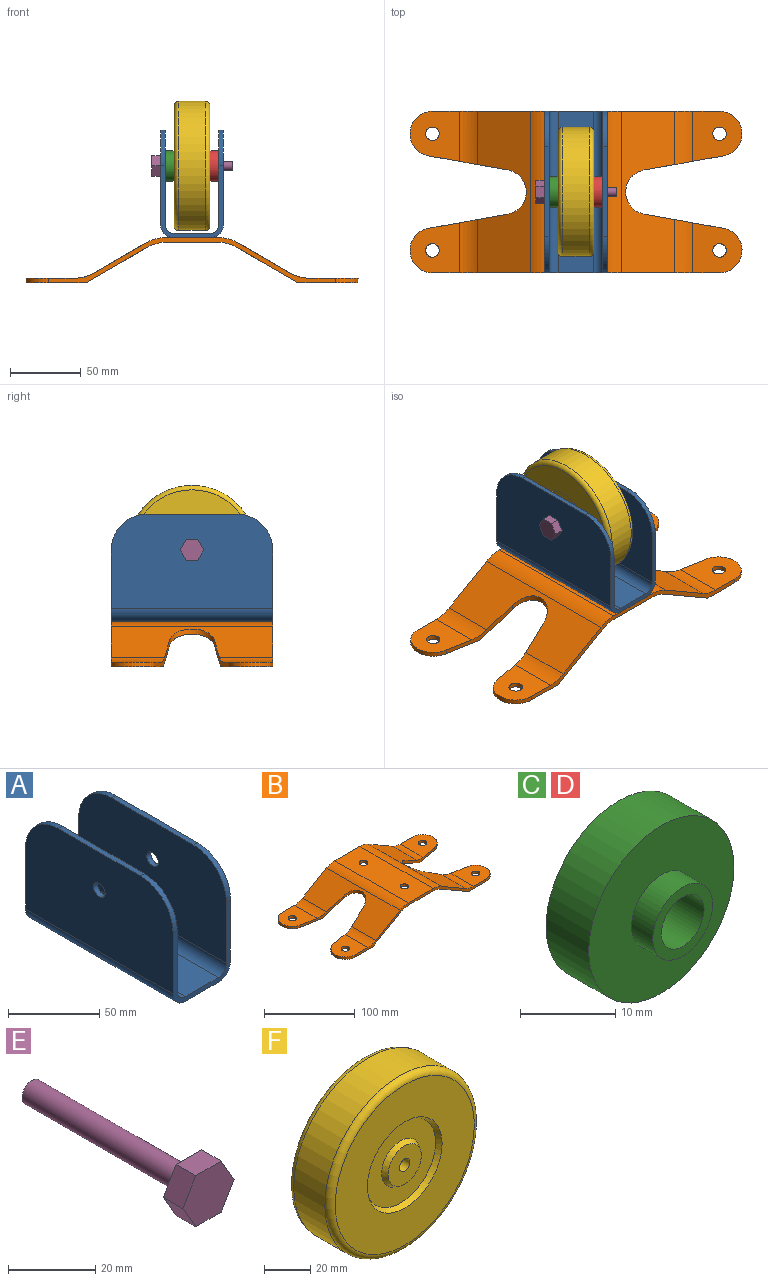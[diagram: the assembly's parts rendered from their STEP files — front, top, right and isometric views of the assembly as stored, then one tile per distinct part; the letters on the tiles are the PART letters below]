
ASSEMBLY  parts=6 mates=11
PART A: 22 faces, bbox 44.5x114.3x76.2 mm
  f0: plane 114.3x25.4mm, normal (0,0,1), area 2760.7mm2, adj f8,f9,f10,f11,f16,f17
  f1: plane 114.3x25.4mm, normal (0,0,-1), area 2760.7mm2, adj f8,f9,f12,f13,f16,f17
  f2: plane 114.3x66.68mm, normal (1,0,0), area 7282mm2, adj f3,f8,f9,f13,f15,f19,f21
  f3: plane 63.5x3.18mm, normal (0,0,1), area 201.6mm2, adj f2,f4,f19,f21
  f4: plane 114.3x66.68mm, normal (-1,0,0), area 7282mm2, adj f3,f8,f9,f10,f15,f19,f21
  f5: plane 114.3x66.68mm, normal (1,0,0), area 7282mm2, adj f6,f8,f9,f11,f14,f18,f20
  f6: plane 63.5x3.18mm, normal (0,0,1), area 201.6mm2, adj f5,f7,f18,f20
  f7: plane 114.3x66.68mm, normal (-1,0,0), area 7282mm2, adj f6,f8,f9,f12,f14,f18,f20
  f8: plane 50.8x44.45mm, normal (0,-1,0), area 421.9mm2, adj f0,f1,f2,f4,f5,f7,f10,f11
  f9: plane 50.8x44.45mm, normal (0,1,0), area 421.9mm2, adj f0,f1,f2,f4,f5,f7,f10,f11
  f10: cylinder r=6.35mm len=114.3mm, axis (0,-1,0), area 1140.1mm2, adj f0,f4,f8,f9
  f11: cylinder r=6.35mm len=114.3mm, axis (0,1,0), area 1140.1mm2, adj f0,f5,f8,f9
  f12: cylinder r=9.53mm len=114.3mm, axis (0,1,0), area 1710.1mm2, adj f1,f7,f8,f9
  f13: cylinder r=9.53mm len=114.3mm, axis (0,-1,0), area 1710.1mm2, adj f1,f2,f8,f9
  f14: cylinder r=4.45mm len=8.89mm, axis (1,0,0), area 88.7mm2, adj f5,f7
  f15: cylinder r=4.45mm len=8.89mm, axis (1,0,0), area 88.7mm2, adj f2,f4
  f16: cylinder r=4.76mm len=9.53mm, axis (0,0,-1), area 95mm2, adj f0,f1
  f17: cylinder r=4.76mm len=9.53mm, axis (0,0,-1), area 95mm2, adj f0,f1
  f18: cylinder r=25.4mm len=25.4mm, axis (-1,0,0), area 126.7mm2, adj f5,f6,f7,f9
  f19: cylinder r=25.4mm len=25.4mm, axis (-1,0,0), area 126.7mm2, adj f2,f3,f4,f9
  f20: cylinder r=25.4mm len=25.4mm, axis (1,0,0), area 126.7mm2, adj f5,f6,f7,f8
  f21: cylinder r=25.4mm len=25.4mm, axis (1,0,0), area 126.7mm2, adj f2,f3,f4,f8
PART B: 40 faces, bbox 235x114.3x31.8 mm
  f0: plane 42.58x36.76mm, normal (0,0,-1), area 1243mm2, adj f2,f8,f15,f16,f17
  f1: plane 42.58x36.76mm, normal (0,0,-1), area 1243mm2, adj f2,f7,f12,f13,f14
  f2: plane 114.3x43.6mm, normal (-0.5,0,-0.87), area 4290.5mm2, adj f0,f1,f12,f14,f15,f17,f18,f39
  f3: plane 114.3x37.19mm, normal (0,0,-1), area 4108.1mm2, adj f12,f17,f21,f22,f38,f39
  f4: plane 114.3x43.6mm, normal (0.5,0,-0.87), area 4290.5mm2, adj f5,f6,f9,f10,f11,f12,f17,f38
  f5: plane 42.58x36.76mm, normal (0,0,-1), area 1243mm2, adj f4,f9,f17,f19,f23
  f6: plane 42.58x36.76mm, normal (0,0,-1), area 1243mm2, adj f4,f11,f12,f20,f24
  f7: cylinder r=4.76mm len=9.53mm, axis (0,0,-1), area 95mm2, adj f1,f31
  f8: cylinder r=4.76mm len=9.53mm, axis (0,0,-1), area 95mm2, adj f0,f25
  f9: plane 55.84x19.06mm, normal (-0.18,0.98,0), area 197.6mm2, adj f4,f5,f10,f19,f28,f30,f37
  f10: cylinder r=15.88mm len=31.26mm, axis (0,0,-1), area 162.3mm2, adj f4,f9,f11,f28
  f11: plane 55.84x19.06mm, normal (-0.18,-0.98,0), area 197.6mm2, adj f4,f6,f10,f20,f28,f29,f33
  f12: plane 203.2x31.75mm, normal (0,1,0), area 701.7mm2, adj f1,f2,f3,f4,f6,f13,f20,f26
  f13: cylinder r=15.88mm len=31.56mm, axis (0,0,-1), area 150.5mm2, adj f1,f12,f14,f31
  f14: plane 55.84x19.06mm, normal (0.18,-0.98,0), area 197.6mm2, adj f1,f2,f13,f18,f26,f31,f32
  f15: plane 55.84x19.06mm, normal (0.18,0.98,0), area 197.6mm2, adj f0,f2,f16,f18,f25,f26,f34
  f16: cylinder r=15.88mm len=31.56mm, axis (0,0,-1), area 150.5mm2, adj f0,f15,f17,f25
  f17: plane 203.2x31.75mm, normal (0,-1,0), area 701.7mm2, adj f0,f2,f3,f4,f5,f16,f19,f25
  f18: cylinder r=15.88mm len=31.26mm, axis (0,0,-1), area 162.3mm2, adj f2,f14,f15,f26
  f19: cylinder r=15.88mm len=31.56mm, axis (0,0,-1), area 150.5mm2, adj f5,f9,f17,f30
  f20: cylinder r=15.88mm len=31.56mm, axis (0,0,-1), area 150.5mm2, adj f6,f11,f12,f29
  f21: cylinder r=4.76mm len=9.53mm, axis (0,0,-1), area 95mm2, adj f3,f27
  f22: cylinder r=4.76mm len=9.53mm, axis (0,0,-1), area 95mm2, adj f3,f27
  f23: cylinder r=4.76mm len=9.53mm, axis (0,0,-1), area 95mm2, adj f5,f30
  f24: cylinder r=4.76mm len=9.53mm, axis (0,0,-1), area 95mm2, adj f6,f29
  f25: plane 35.4x34.93mm, normal (0,0,1), area 966.8mm2, adj f8,f15,f16,f17,f34
  f26: plane 114.3x37.71mm, normal (0.5,0,0.87), area 3744.8mm2, adj f12,f14,f15,f17,f18,f32,f34,f35
  f27: plane 114.3x38.89mm, normal (0,0,1), area 4302.6mm2, adj f12,f17,f21,f22,f35,f36
  f28: plane 114.3x37.71mm, normal (-0.5,0,0.87), area 3744.8mm2, adj f9,f10,f11,f12,f17,f33,f36,f37
  f29: plane 35.4x34.93mm, normal (0,0,1), area 966.8mm2, adj f11,f12,f20,f24,f33
  f30: plane 35.4x34.93mm, normal (0,0,1), area 966.8mm2, adj f9,f17,f19,f23,f37
  f31: plane 35.4x34.93mm, normal (0,0,1), area 966.8mm2, adj f7,f12,f13,f14,f32
  f32: cylinder r=25.4mm len=37.66mm, axis (0,-1,0), area 486.2mm2, adj f12,f14,f26,f31
  f33: cylinder r=25.4mm len=37.66mm, axis (0,-1,0), area 486.2mm2, adj f11,f12,f28,f29
  f34: cylinder r=25.4mm len=37.66mm, axis (0,-1,0), area 486.2mm2, adj f15,f17,f25,f26
  f35: cylinder r=25.4mm len=114.3mm, axis (0,1,0), area 1520.1mm2, adj f12,f17,f26,f27
  f36: cylinder r=25.4mm len=114.3mm, axis (0,-1,0), area 1520.1mm2, adj f12,f17,f27,f28
  f37: cylinder r=25.4mm len=37.66mm, axis (0,-1,0), area 486.2mm2, adj f9,f17,f28,f30
  f38: cylinder r=25.4mm len=114.3mm, axis (0,-1,0), area 1520.1mm2, adj f3,f4,f12,f17
  f39: cylinder r=25.4mm len=114.3mm, axis (0,1,0), area 1520.1mm2, adj f2,f3,f12,f17
PART C: 6 faces, bbox 21.6x9.5x21.6 mm
  f0: plane 8.89x8.89mm, normal (0,-1,0), area 30.4mm2, adj f1,f5
  f1: cylinder r=3.17mm len=9.53mm, axis (0,1,0), area 190mm2, adj f0,f2
  f2: plane 21.59x21.59mm, normal (0,1,0), area 334.4mm2, adj f1,f3
  f3: cylinder r=10.79mm len=21.59mm, axis (0,1,0), area 430.7mm2, adj f2,f4
  f4: plane 21.59x21.59mm, normal (0,-1,0), area 304mm2, adj f3,f5
  f5: cylinder r=4.45mm len=8.89mm, axis (0,1,0), area 88.7mm2, adj f0,f4
PART D: same geometry as C
PART E: 10 faces, bbox 16.5x57.2x14.3 mm
  f0: plane 7.14x6.35mm, normal (-0.87,0,0.5), area 52.4mm2, adj f1,f5,f6,f7
  f1: plane 7.14x6.35mm, normal (-0.87,0,-0.5), area 52.4mm2, adj f0,f2,f6,f7
  f2: plane 8.25x6.35mm, normal (0,0,-1), area 52.4mm2, adj f1,f3,f6,f7
  f3: plane 7.14x6.35mm, normal (0.87,0,-0.5), area 52.4mm2, adj f2,f4,f6,f7
  f4: plane 7.14x6.35mm, normal (0.87,0,0.5), area 52.4mm2, adj f3,f5,f6,f7
  f5: plane 8.25x6.35mm, normal (0,0,1), area 52.4mm2, adj f0,f4,f6,f7
  f6: plane 16.5x14.29mm, normal (0,-1,0), area 176.8mm2, adj f0,f1,f2,f3,f4,f5
  f7: plane 16.5x14.29mm, normal (0,1,0), area 145.1mm2, adj f0,f1,f2,f3,f4,f5,f8
  f8: cylinder r=3.17mm len=50.8mm, axis (0,-1,0), area 1013.4mm2, adj f7,f9
  f9: plane 6.35x6.35mm, normal (0,1,0), area 31.7mm2, adj f8
PART F: 14 faces, bbox 99x25.4x99 mm
  f0: cone r=21.39mm half-angle=30deg, axis (0,-1,0), area 407.8mm2, adj f1,f13
  f1: plane 42.79x42.79mm, normal (0,-1,0), area 1013.2mm2, adj f0,f2
  f2: cone r=10.16mm half-angle=30deg, axis (0,1,0), area 200.7mm2, adj f1,f3
  f3: plane 20.32x20.32mm, normal (0,-1,0), area 292.6mm2, adj f2,f4
  f4: cylinder r=3.17mm len=25.4mm, axis (0,1,0), area 506.7mm2, adj f3,f5
  f5: plane 20.32x20.32mm, normal (0,1,0), area 292.6mm2, adj f4,f6
  f6: cone r=10.16mm half-angle=30deg, axis (0,-1,0), area 200.7mm2, adj f5,f7
  f7: plane 42.79x42.79mm, normal (0,1,0), area 1013.2mm2, adj f6,f8
  f8: cone r=21.39mm half-angle=30deg, axis (0,1,0), area 407.8mm2, adj f7,f9
  f9: plane 85.09x85.09mm, normal (0,1,0), area 4044.8mm2, adj f8,f10
  f10: torus R=42.55mm, axis (0,1,0), area 1396.5mm2, adj f9,f11
  f11: cylinder r=45.72mm len=91.44mm, axis (0,1,0), area 5472.4mm2, adj f10,f12
  f12: torus R=42.55mm, axis (0,1,0), area 1396.5mm2, adj f11,f13
  f13: plane 85.09x85.09mm, normal (0,-1,0), area 4044.8mm2, adj f0,f12
PLACE A rot(axis=(-0.05,0.61,0.79),0deg) t=(28.07,1.25,53.88)mm
PLACE B rot(axis=(-0.05,0.61,0.79),0deg) t=(28.07,1.25,50.71)mm
PLACE C rot(axis=(-0.58,-0.58,-0.58),120deg) t=(15.37,1.25,104.68)mm
PLACE D rot(axis=(0.58,-0.58,0.58),120deg) t=(40.77,1.25,104.68)mm
PLACE E rot(axis=(0,0,-1),90deg) t=(5.84,1.25,104.68)mm
PLACE F rot(axis=(0,0,1),90deg) t=(28.07,1.25,104.68)mm
MATE cylindrical E.f8 <-> A.f14  axis (-1,0,0) through (56.64,1.25,104.68)mm
MATE planar B.f27 <-> A.f1  axis (0,0,1) through (28.07,1.25,53.88)mm
MATE cylindrical C.f1 <-> A.f14  axis (1,0,0) through (5.84,1.25,104.68)mm
MATE cylindrical A.f17 <-> B.f22  axis (0,0,1) through (28.07,33,57.06)mm
MATE planar A.f5 <-> C.f1  axis (1,0,0) through (9.02,1.25,95.62)mm
MATE cylindrical A.f16 <-> B.f21  axis (0,0,-1) through (28.07,-30.5,55.47)mm
MATE slider F.f0 <-> C.f1  axis (1,0,0) through (40.77,1.25,104.68)mm
MATE cylindrical D.f1 <-> A.f14  axis (-1,0,0) through (40.77,1.25,104.68)mm
MATE planar F.f0 <-> D.f1  axis (1,0,0) through (40.77,1.25,104.68)mm
MATE planar E.f7 <-> A.f7  axis (1,0,0) through (5.84,-2.87,111.82)mm
MATE planar D.f1 <-> A.f4  axis (1,0,0) through (47.12,1.25,104.68)mm
